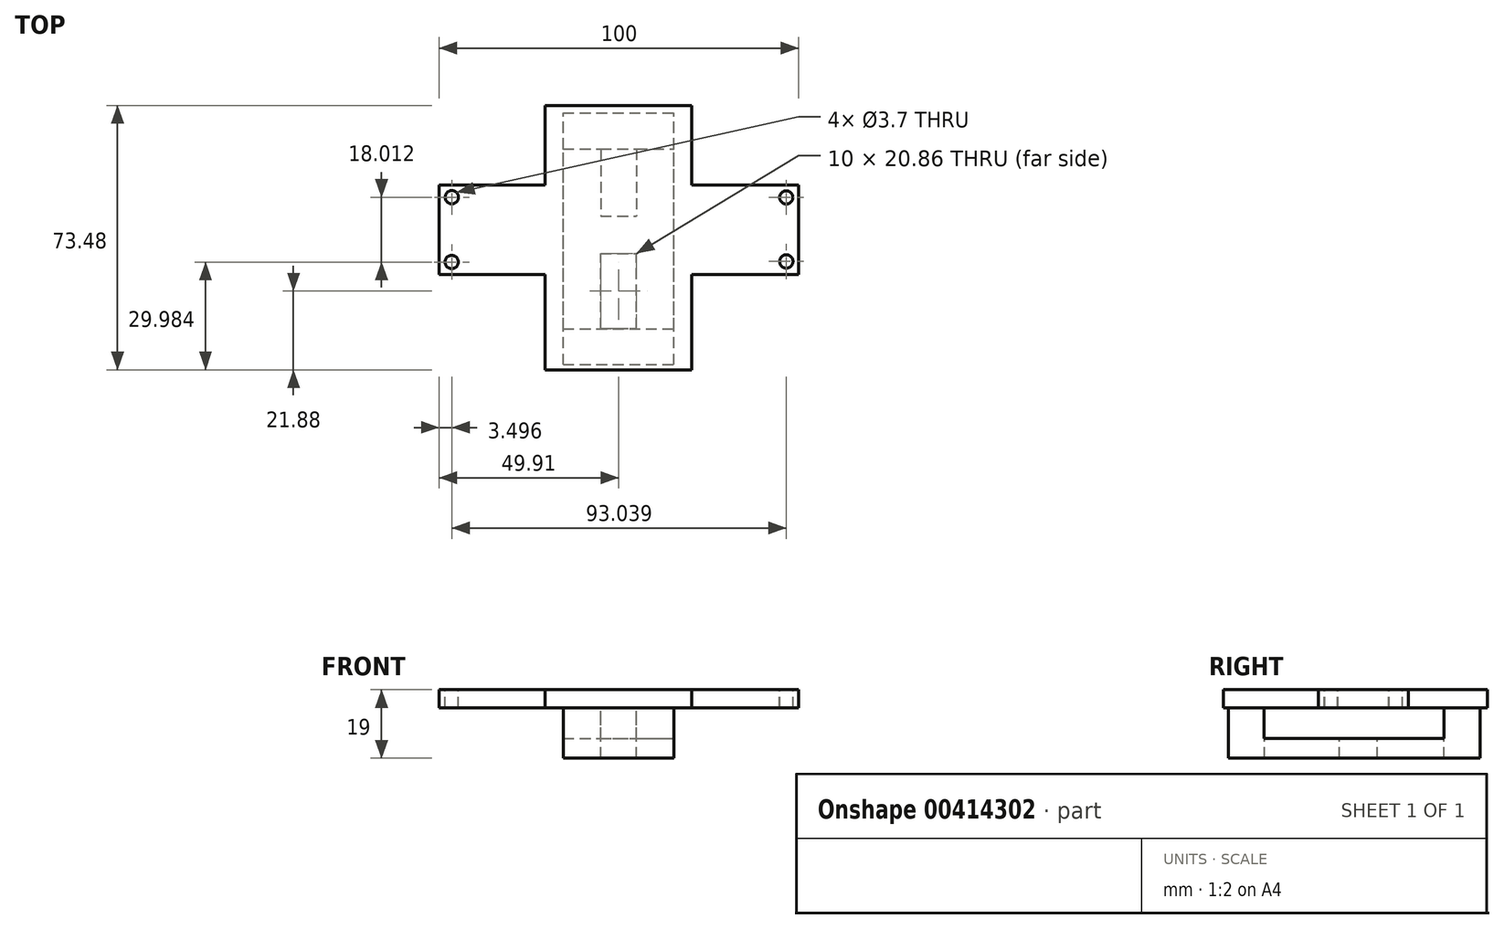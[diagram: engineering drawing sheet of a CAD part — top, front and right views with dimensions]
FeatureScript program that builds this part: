
annotation { "Feature Type Name" : "Feature", "Feature Type Description" : "" }
export const myFeature = defineFeature(function(context is Context, id is Id, definition is map)
    precondition{}
    {
        {
            var Q0;
            Q0=qCreatedBy(makeId("Top.planeOp"),FACE);
            var sketch = newSketch(context, id + "F0", { "sketchPlane" : qUnion([Q0])});
            skLineSegment(sketch, "E0.0", {"start": v(-15.4, 53.06) * mm, "end": v(-15.4, -20.42) * mm});
            skLineSegment(sketch, "E0.1", {"start": v(25.36, 53.06) * mm, "end": v(-15.4, 53.06) * mm});
            skLineSegment(sketch, "E0.2", {"start": v(25.36, -20.42) * mm, "end": v(25.36, 53.06) * mm});
            skLineSegment(sketch, "E0.3", {"start": v(-15.4, -20.42) * mm, "end": v(25.36, -20.42) * mm});
            skSolve(sketch);
        }
        {
            var Q0;
            Q0=makeQuery(id+"F0.imprint","IMPRINT",FACE,{"disambiguationData":[TD([[makeQuery(id+"F0.imprint","IMPRINT",EDGE,{"derivedFrom":sQuery(id+"F0.wireOp",EDGE,"E0.0")}),1.0]])]});
            extrude(context, id + "F1", {"entities" : qUnion([Q0]), "oppositeDirection" : true, "depth" : 5 * mm});
        }
        {
            var Q0;
            Q0=makeQuery(id+"F1.opExtrude","CAP_FACE",FACE,{"disambiguationData":[OSD([sQuery(id+"F0.wireOp",EDGE,"E0.0"),sQuery(id+"F0.wireOp",EDGE,"E0.1"),sQuery(id+"F0.wireOp",EDGE,"E0.2"),sQuery(id+"F0.wireOp",EDGE,"E0.3"),sQuery(id+"F0.wireOp",EDGE,"AwGas1L0-Tx7c-sK6K-lToC-j4NMW9GVDTDE.right")])],"isStart":false});
            var sketch = newSketch(context, id + "F2", { "sketchPlane" : qUnion([Q0])});
            skLineSegment(sketch, "E1.bottom", {"start": v(-10.4, 18.97) * mm, "end": v(20.4, 18.97) * mm});
            skLineSegment(sketch, "E1.top", {"start": v(-10.4, -51.03) * mm, "end": v(20.4, -51.03) * mm});
            skLineSegment(sketch, "E1.left", {"start": v(-10.4, 18.97) * mm, "end": v(-10.4, -51.03) * mm});
            skLineSegment(sketch, "E1.right", {"start": v(20.4, 18.97) * mm, "end": v(20.4, -51.03) * mm});
            skLineSegment(sketch, "E2", {"start": v(5, -41.03) * mm, "end": v(10, -41.03) * mm});
            skLineSegment(sketch, "E3", {"start": v(5, 8.97) * mm, "end": v(10, 8.97) * mm});
            skLineSegment(sketch, "E4", {"start": v(5, -41.03) * mm, "end": v(0, -41.03) * mm});
            skLineSegment(sketch, "E5", {"start": v(5, 8.97) * mm, "end": v(0, 8.97) * mm});
            skLineSegment(sketch, "E6", {"start": v(0, -11.89) * mm, "end": v(10, -11.89) * mm});
            skLineSegment(sketch, "E7", {"start": v(0, -22.37) * mm, "end": v(10, -22.37) * mm});
            skLineSegment(sketch, "E8", {"start": v(10, 8.97) * mm, "end": v(10, -11.89) * mm});
            skLineSegment(sketch, "E9", {"start": v(0, 8.97) * mm, "end": v(0, -11.89) * mm});
            skLineSegment(sketch, "E10", {"start": v(10, -41.03) * mm, "end": v(10, -22.37) * mm});
            skLineSegment(sketch, "E11", {"start": v(0, -41.03) * mm, "end": v(0, -22.37) * mm});
            skSolve(sketch);
        }
        {
            var Q0;
            Q0=qSketchRegion(id+"F2",true);
            extrude(context, id + "F3", {"entities" : qUnion([Q0]), "operationType" : NewBodyOperationType.ADD, "depth" : 14 * mm});
        }
        {
            var Q0;
            {var subQ0=sQuery(id+"F0.wireOp",EDGE,"AwGas1L0-Tx7c-sK6K-lToC-j4NMW9GVDTDE.right");var subQ1=sQuery(id+"F0.wireOp",EDGE,"E0.0");var subQ2=sQuery(id+"F0.wireOp",EDGE,"E0.1");var subQ3=sQuery(id+"F0.wireOp",EDGE,"E0.2");var subQ4=sQuery(id+"F0.wireOp",EDGE,"E0.3");Q0=makeQuery(id+"F3.boolean.opBoolean","SPLIT",FACE,{"disambiguationData":[TD([makeQuery(id+"F1.opExtrude","SWEPT_FACE",FACE,{"disambiguationData":[OSD([subQ2])]})])],"derivedFrom":makeQuery(id+"F1.opExtrude","CAP_FACE",FACE,{"disambiguationData":[OSD([subQ1,subQ2,subQ3,subQ4,subQ0])],"isStart":false})});}
            var sketch = newSketch(context, id + "F4", { "sketchPlane" : qUnion([Q0])});
            skLineSegment(sketch, "E12.bottom", {"start": v(-14.6, 9.01) * mm, "end": v(20.4, 9.01) * mm});
            skLineSegment(sketch, "E12.top", {"start": v(-14.6, -41) * mm, "end": v(20.4, -41) * mm});
            skLineSegment(sketch, "E12.left", {"start": v(-14.6, 9.01) * mm, "end": v(-14.6, -41) * mm});
            skLineSegment(sketch, "E12.right", {"start": v(20.4, 9.01) * mm, "end": v(20.4, -41) * mm});
            skSolve(sketch);
        }
        {
            var Q0;
            Q0=qSketchRegion(id+"F4",true);
            var Q1;
            Q1=sQuery(id+"F4.wireOp",EDGE,"E12.left");
            extrude(context, id + "F5", {"entities" : qUnion([Q0]), "operationType" : NewBodyOperationType.REMOVE, "surfaceEntities" : qUnion([Q1]), "depth" : 8.5 * mm});
        }
        {
            var Q0;
            {var subQ0=sQuery(id+"F0.wireOp",EDGE,"E0.3");var subQ1=sQuery(id+"F0.wireOp",EDGE,"E0.2");var subQ2=sQuery(id+"F0.wireOp",EDGE,"E0.1");var subQ3=sQuery(id+"F0.wireOp",EDGE,"E0.0");var subQ4=makeQuery(id+"F1.opExtrude","CAP_FACE",FACE,{"disambiguationData":[OSD([subQ3,subQ2,subQ1,subQ0])],"isStart":false});Q0=makeQuery(id+"F5.boolean.opBoolean","MERGE",FACE,{"derivedFrom":[makeQuery(id+"F3.boolean.opBoolean","SPLIT",FACE,{"disambiguationData":[TD([makeQuery(id+"F1.opExtrude","SWEPT_FACE",FACE,{"disambiguationData":[OSD([subQ3])]})])],"derivedFrom":subQ4}),makeQuery(id+"F3.boolean.opBoolean","SPLIT",FACE,{"disambiguationData":[TD([makeQuery(id+"F3.opExtrude","SWEPT_FACE",FACE,{"disambiguationData":[OSD([sQuery(id+"F2.wireOp",EDGE,"E7")])]})])],"derivedFrom":subQ4}),makeQuery(id+"F3.boolean.opBoolean","SPLIT",FACE,{"disambiguationData":[TD([makeQuery(id+"F3.opExtrude","SWEPT_FACE",FACE,{"disambiguationData":[OSD([sQuery(id+"F2.wireOp",EDGE,"E6")])]})])],"derivedFrom":subQ4}),makeQuery(id+"F5.opExtrude","CAP_FACE",FACE,{"disambiguationData":[OSD([sQuery(id+"F4.wireOp",EDGE,"E12.bottom"),sQuery(id+"F4.wireOp",EDGE,"E12.top"),sQuery(id+"F4.wireOp",EDGE,"E12.left"),sQuery(id+"F4.wireOp",EDGE,"E12.right")])],"isStart":true})]});}
            var sketch = newSketch(context, id + "F6", { "sketchPlane" : qUnion([Q0])});
            skLineSegment(sketch, "E13.bottom", {"start": v(-44.9, -31.01) * mm, "end": v(55.1, -31.01) * mm});
            skLineSegment(sketch, "E13.top", {"start": v(-44.9, -6.1) * mm, "end": v(55.1, -6.1) * mm});
            skLineSegment(sketch, "E13.left", {"start": v(-44.9, -31.01) * mm, "end": v(-44.9, -6.1) * mm});
            skLineSegment(sketch, "E13.right", {"start": v(55.1, -31.01) * mm, "end": v(55.1, -6.1) * mm});
            skPoint(sketch, "E14.endSnap0", {"position": v(4.98, -53.06) * mm});
            skSolve(sketch);
        }
        {
            var Q0;
            Q0=qSketchRegion(id+"F6",true);
            extrude(context, id + "F7", {"entities" : qUnion([Q0]), "operationType" : NewBodyOperationType.ADD, "oppositeDirection" : true, "depth" : 5 * mm});
        }
        {
            var Q0;
            Q0=makeQuery(id+"F7.boolean.opBoolean","MERGE",FACE,{"derivedFrom":[makeQuery(id+"F1.opExtrude","CAP_FACE",FACE,{"disambiguationData":[OSD([sQuery(id+"F0.wireOp",EDGE,"E0.0"),sQuery(id+"F0.wireOp",EDGE,"E0.1"),sQuery(id+"F0.wireOp",EDGE,"E0.2"),sQuery(id+"F0.wireOp",EDGE,"E0.3")])],"isStart":true}),makeQuery(id+"F7.opExtrude","CAP_FACE",FACE,{"disambiguationData":[OSD([sQuery(id+"F6.wireOp",EDGE,"E13.bottom"),sQuery(id+"F6.wireOp",EDGE,"E13.top"),sQuery(id+"F6.wireOp",EDGE,"E13.left"),sQuery(id+"F6.wireOp",EDGE,"E13.right")])],"isStart":false})]});
            var sketch = newSketch(context, id + "F8", { "sketchPlane" : qUnion([Q0])});
            skCircle(sketch, "E15", {"center": v(-41.39, 27.58) * mm, "radius": 1.85 * mm});
            skCircle(sketch, "E16", {"center": v(51.6, 27.51) * mm, "radius": 1.85 * mm});
            skLineSegment(sketch, "E17", {"start": v(-44.9, 31.01) * mm, "end": v(-41.4, 31.01) * mm});
            skCircle(sketch, "E18", {"center": v(-41.41, 9.56) * mm, "radius": 1.85 * mm});
            skCircle(sketch, "E19", {"center": v(51.62, 9.7) * mm, "radius": 1.85 * mm});
            skSolve(sketch);
        }
        {
            var Q0;
            Q0=qSketchRegion(id+"F8",true);
            extrude(context, id + "F9", {"entities" : qUnion([Q0]), "operationType" : NewBodyOperationType.REMOVE, "oppositeDirection" : true, "depth" : 25.4 * mm});
        }
    });
